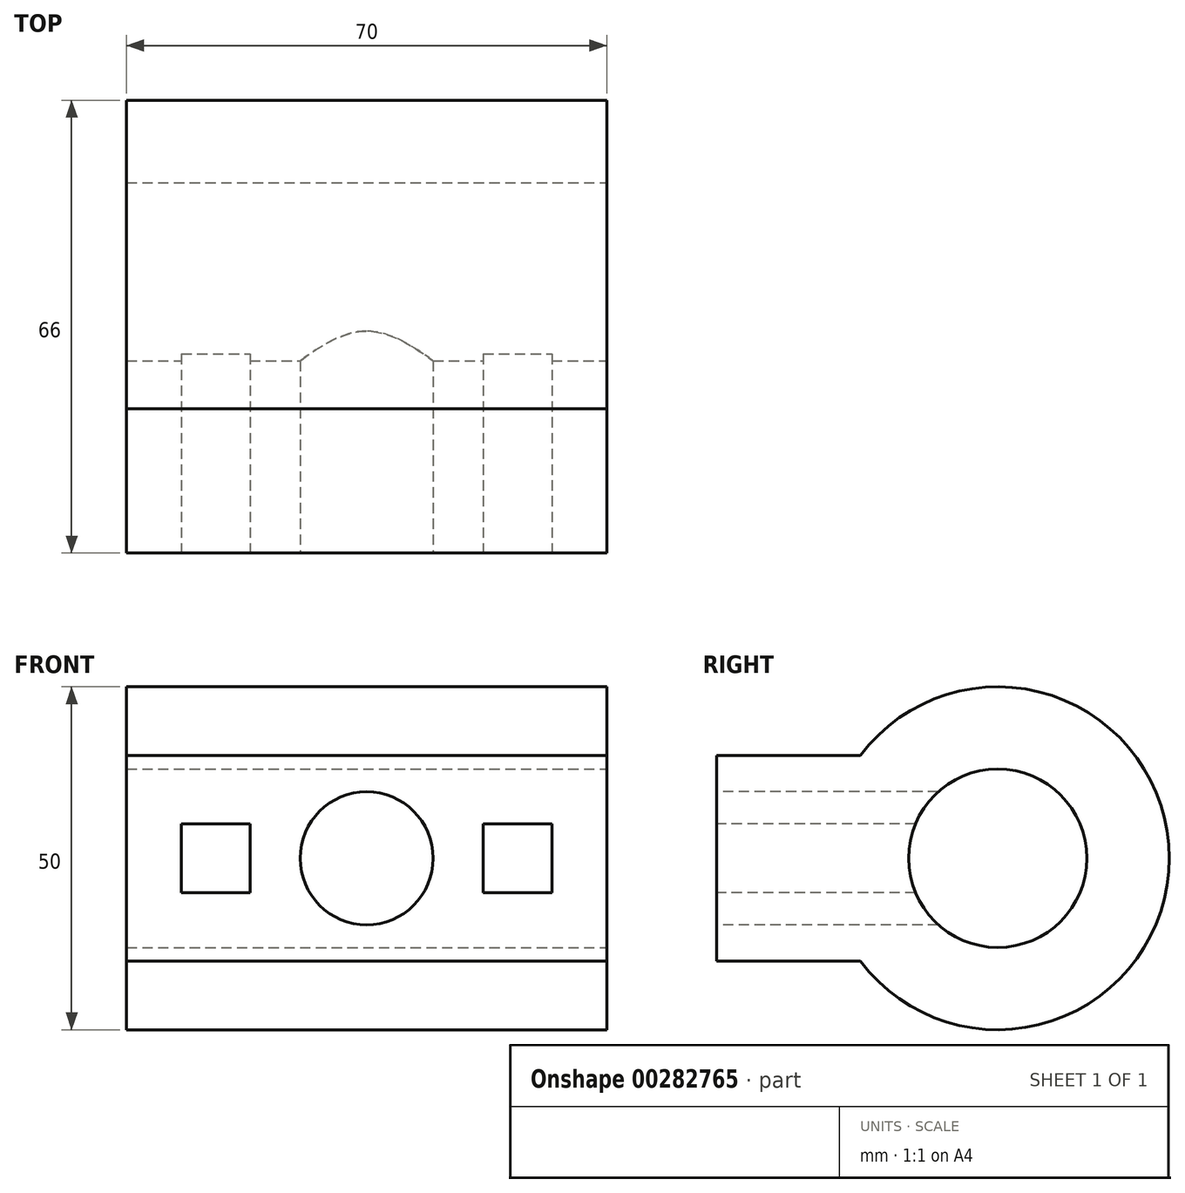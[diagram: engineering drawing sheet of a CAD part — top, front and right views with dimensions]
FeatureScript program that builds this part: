
annotation { "Feature Type Name" : "Feature", "Feature Type Description" : "" }
export const myFeature = defineFeature(function(context is Context, id is Id, definition is map)
    precondition{}
    {
        {
            var Q0;
            Q0=qCreatedBy(makeId("Front.planeOp"),FACE);
            var sketch = newSketch(context, id + "F0", { "sketchPlane" : qUnion([Q0])});
            skLineSegment(sketch, "E0.bottom", {"start": v(0, 0) * mm, "end": v(70, 0) * mm});
            skLineSegment(sketch, "E0.top", {"start": v(0, 30) * mm, "end": v(70, 30) * mm});
            skLineSegment(sketch, "E0.left", {"start": v(0, 0) * mm, "end": v(0, 30) * mm});
            skLineSegment(sketch, "E0.right", {"start": v(70, 0) * mm, "end": v(70, 30) * mm});
            skSolve(sketch);
        }
        {
            var Q0;
            Q0=makeQuery(id+"F0.imprint","IMPRINT",FACE,{"disambiguationData":[TD([[makeQuery(id+"F0.imprint","IMPRINT",EDGE,{"derivedFrom":sQuery(id+"F0.wireOp",EDGE,"E0.bottom")}),1.0]])]});
            extrude(context, id + "F1", {"entities" : qUnion([Q0]), "oppositeDirection" : true, "depth" : 41 * mm});
        }
        {
            var Q0;
            Q0=makeQuery(id+"F1.opExtrude","CAP_FACE",FACE,{"disambiguationData":[OSD([sQuery(id+"F0.wireOp",EDGE,"E0.bottom"),sQuery(id+"F0.wireOp",EDGE,"E0.top"),sQuery(id+"F0.wireOp",EDGE,"E0.left"),sQuery(id+"F0.wireOp",EDGE,"E0.right")])],"isStart":true});
            var sketch = newSketch(context, id + "F2", { "sketchPlane" : qUnion([Q0])});
            skLineSegment(sketch, "E1.bottom", {"start": v(8, 10) * mm, "end": v(18, 10) * mm});
            skLineSegment(sketch, "E1.top", {"start": v(8, 20) * mm, "end": v(18, 20) * mm});
            skLineSegment(sketch, "E1.left", {"start": v(8, 10) * mm, "end": v(8, 20) * mm});
            skLineSegment(sketch, "E1.right", {"start": v(18, 10) * mm, "end": v(18, 20) * mm});
            skLineSegment(sketch, "E2.top", {"start": v(70, 10) * mm, "end": v(62, 10) * mm});
            skLineSegment(sketch, "E3.bottom", {"start": v(62, 10) * mm, "end": v(52, 10) * mm});
            skLineSegment(sketch, "E3.top", {"start": v(62, 20) * mm, "end": v(52, 20) * mm});
            skLineSegment(sketch, "E3.left", {"start": v(62, 10) * mm, "end": v(62, 20) * mm});
            skLineSegment(sketch, "E3.right", {"start": v(52, 10) * mm, "end": v(52, 20) * mm});
            skCircle(sketch, "E4", {"center": v(35, 15) * mm, "radius": 9.7 * mm});
            skSolve(sketch);
        }
        {
            var Q0;
            Q0=makeQuery(id+"F2.imprint","IMPRINT",FACE,{"disambiguationData":[TD([[makeQuery(id+"F2.imprint","IMPRINT",EDGE,{"derivedFrom":sQuery(id+"F2.wireOp",EDGE,"E1.bottom")}),1.0]])]});
            var Q1;
            Q1=makeQuery(id+"F2.imprint","IMPRINT",FACE,{"disambiguationData":[TD([[makeQuery(id+"F2.imprint","IMPRINT",EDGE,{"derivedFrom":sQuery(id+"F2.wireOp",EDGE,"E4")}),1.0]])]});
            var Q2;
            Q2=makeQuery(id+"F2.imprint","IMPRINT",FACE,{"disambiguationData":[TD([[makeQuery(id+"F2.imprint","IMPRINT",EDGE,{"derivedFrom":sQuery(id+"F2.wireOp",EDGE,"E3.bottom")}),-1.0]])]});
            extrude(context, id + "F3", {"entities" : qUnion([Q0, Q1, Q2]), "operationType" : NewBodyOperationType.REMOVE, "oppositeDirection" : true, "depth" : 41 * mm});
        }
        {
            var Q0;
            Q0=makeQuery(id+"F1.opExtrude","SWEPT_FACE",FACE,{"disambiguationData":[OSD([sQuery(id+"F0.wireOp",EDGE,"E0.right")])]});
            var sketch = newSketch(context, id + "F4", { "sketchPlane" : qUnion([Q0])});
            skCircle(sketch, "E5", {"center": v(41, 15) * mm, "radius": 25 * mm});
            skCircle(sketch, "E6", {"center": v(41, 15) * mm, "radius": 13 * mm});
            skSolve(sketch);
        }
        {
            var Q0;
            {var subQ0=sQuery(id+"F4.wireOp",EDGE,"E6");var subQ1=makeQuery(id+"F1.opExtrude","CAP_EDGE",EDGE,{"disambiguationData":[OSD([sQuery(id+"F0.wireOp",EDGE,"E0.right")])],"isStart":false});var subQ2=makeQuery(id+"F4.imprint","INTERSECT",VERTEX,{"disambiguationData":[OD(0.0)],"derivedFrom":[subQ1,subQ0]});Q0=makeQuery(id+"F4.imprint","IMPRINT",FACE,{"disambiguationData":[TD([[makeQuery(id+"F4.imprint","IMPRINT",EDGE,{"disambiguationData":[TD([[subQ2,-1.0]])],"derivedFrom":subQ0}),1.0]])]});}
            var Q1;
            {var subQ0=sQuery(id+"F4.wireOp",EDGE,"E6");var subQ1=makeQuery(id+"F1.opExtrude","CAP_EDGE",EDGE,{"disambiguationData":[OSD([sQuery(id+"F0.wireOp",EDGE,"E0.right")])],"isStart":false});var subQ2=makeQuery(id+"F4.imprint","INTERSECT",VERTEX,{"disambiguationData":[OD(0.0)],"derivedFrom":[subQ1,subQ0]});Q1=makeQuery(id+"F4.imprint","IMPRINT",FACE,{"disambiguationData":[TD([[makeQuery(id+"F4.imprint","IMPRINT",EDGE,{"disambiguationData":[TD([[subQ2,1.0]])],"derivedFrom":subQ0}),1.0]])]});}
            var Q2;
            {var subQ0=sQuery(id+"F0.wireOp",EDGE,"E0.right");var subQ1=makeQuery(id+"F1.opExtrude","CAP_EDGE",EDGE,{"disambiguationData":[OSD([subQ0])],"isStart":false});var subQ6=sQuery(id+"F4.wireOp",EDGE,"E6");var subQ7=makeQuery(id+"F4.imprint","INTERSECT",VERTEX,{"disambiguationData":[OD(0.0)],"derivedFrom":[subQ1,subQ6]});Q2=makeQuery(id+"F4.imprint","IMPRINT",FACE,{"disambiguationData":[TD([[makeQuery(id+"F4.imprint","IMPRINT",EDGE,{"disambiguationData":[TD([[subQ7,-1.0]])],"derivedFrom":subQ6}),-1.0]])]});}
            extrude(context, id + "F5", {"entities" : qUnion([Q0, Q1, Q2]), "operationType" : NewBodyOperationType.ADD, "oppositeDirection" : true, "depth" : 70 * mm});
        }
        {
            var Q0;
            {var subQ0=sQuery(id+"F4.wireOp",EDGE,"E6");var subQ1=makeQuery(id+"F1.opExtrude","CAP_EDGE",EDGE,{"disambiguationData":[OSD([sQuery(id+"F0.wireOp",EDGE,"E0.right")])],"isStart":false});var subQ2=makeQuery(id+"F4.imprint","INTERSECT",VERTEX,{"disambiguationData":[OD(0.0)],"derivedFrom":[subQ1,subQ0]});Q0=makeQuery(id+"F4.imprint","IMPRINT",FACE,{"disambiguationData":[TD([[makeQuery(id+"F4.imprint","IMPRINT",EDGE,{"disambiguationData":[TD([[subQ2,-1.0]])],"derivedFrom":subQ0}),1.0]])]});}
            var Q1;
            {var subQ0=sQuery(id+"F4.wireOp",EDGE,"E6");var subQ1=makeQuery(id+"F1.opExtrude","CAP_EDGE",EDGE,{"disambiguationData":[OSD([sQuery(id+"F0.wireOp",EDGE,"E0.right")])],"isStart":false});var subQ2=makeQuery(id+"F4.imprint","INTERSECT",VERTEX,{"disambiguationData":[OD(0.0)],"derivedFrom":[subQ1,subQ0]});Q1=makeQuery(id+"F4.imprint","IMPRINT",FACE,{"disambiguationData":[TD([[makeQuery(id+"F4.imprint","IMPRINT",EDGE,{"disambiguationData":[TD([[subQ2,1.0]])],"derivedFrom":subQ0}),1.0]])]});}
            extrude(context, id + "F6", {"entities" : qUnion([Q0, Q1]), "operationType" : NewBodyOperationType.REMOVE, "oppositeDirection" : true, "depth" : 70 * mm});
        }
    });
